# Revit family: Storage-Freestanding-Teknion-JNFMP-Mobile_Pedestal_with_Seat-R2018
name_source: partatom
category: Furniture
revit_build: Autodesk Revit 2018 (Build: 20190510_1515(x64)
units: mm (PartAtom-declared; Revit-internal decimal feet)

## family parameters
Always vertical = Yes
Cut with Voids When Loaded = No
OmniClass Number = 23.40.20.00
OmniClass Title = General Furniture and Specialties
Room Calculation Point = No
Shared = Yes
Work Plane-Based = No

## types (2) — shared parameters
Assembly Code = E2020200
Description = Mobile Pedestal with Seat - Felt
Manufacturer = Teknion
Manufacturer Fax = 416.661.4586
Part Number = JNFMP
Product Documentation Link = http://www.teknion.com
Product Line = Expansion Cityline
Product Page URL = http://www.teknion.com
Series = Expansion Cityline
Sustainability Data = http://www.teknion.com
URL = www.teknion.com
Unit Weight URL = http://www.teknion.com
Warranty = http://www.teknion.com

## per-type parameters (varying)
| type | Front Finish | Has Metal Front Style | Has Solid Front Style | Model |
| Metal | Mica - Teknion - V - Satin - Very White | Yes | No | JNFMPM |
| Solid | Source Laminate - Teknion - XS - Storm White | No | Yes | JNFMPS |

## geometry (parser evidence)
native form markers: Sweep x2
no freeform markers — native parametric forms only
